# Revit family: UPA
name_source: partatom
category: Mechanical Equipment
units: mm (PartAtom-declared; Revit-internal decimal feet)

## family parameters
Always vertical = Yes
Cut with Voids When Loaded = No
OmniClass Number = 23.40.40.11.17
OmniClass Title = Refrigerated Cases
Part Type = Normal
Room Calculation Point = No
Round Connector Dimension = Use Radius
Shared = No
Work Plane-Based = Yes

## types (1)
- UPA-8'
    10" Shelf = Yes
    8" Shelf = Yes
    ANTI CON AMPS = 0 A
    BOTTOM ELECTRICAL = Yes
    BOTTOM REFRIGERATION PIPING = Yes
    CENTER LINE = 48"
    Certifications = NSF 7, UL471, CSA
    DATE = 05/11/2017
    DEFROST AMPS = 0 A
    DESIGNERS NAME = SHIDDRAMESH
    DISCHARGE AIR TEMP = 0 °F
    DISCHARGE AIR VELOCITY = -(FPM)
    DRAIN HEATERS AMPS = 0 A
    DRAIN LINE CONNECTION = SANITARY CONNECTION
    DRAIN LINE DIAMETER = 2"
    DRAIN PIPE TYPE = PVC
    DRAIN PIPING = Yes
    DRIP PAN PLUMB TYPE = HARD
    Default Elevation = 48"
    Defrost Num Day = 0
    Defrost Termination = - °F
    Defrost Type = TIMED-OFF DEFROST
    Description = Mobile Single-Deck Self-Contained Merchandiser
    Door = Door 8' : OGM-8'
    END PANEL = <By Category>
    EQUIPMENT DESCRIPTION = Mobile Single-Deck Self-Contained Merchandiser
    EQUIPMENT MARK = UPA
    Ends = Yes
    Evap Temp = 0
    GLASS = Glass
    HIGH EFFICIENCY FANS AMPS = 0 A
    Height = 49 1/4"
    Item Description = Mobile Single-Deck Self-Contained Merchandiser
    LEFT END = Yes
    LF STD END = Yes
    LIGHT AMPS = 0 A
    LIQUID LINE CONNECTION = LIQUID LINE CONNECTION
    LIQUID LINE DIAMETER = 0"
    LIQUID LINE RADIUS = 0"
    LOAD 1 CLASSIFICATION = Lighting
    LOAD 1 DESCRIPTION = LIGHTS - STANDARD POWER (SHELF or CORNICE)
    LOAD 1 PLUG TYPE = HARDWIRED
    LOAD 1 POLES = 1
    LOAD 1 VOLTAGE = 120 V
    LOAD 1 WATTAGE = 0 W
    LOAD 2 CLASSIFICATION = Motor
    LOAD 2 DESCRIPTION = HIGH EFFICIENCY FANS CONNECTION
    LOAD 2 PLUG TYPE = HARDWIRED
    LOAD 2 POLES = 1
    LOAD 2 VOLTAGE = 120 V
    LOAD 2 WATTAGE = 0 W
    LOAD 3 CLASSIFICATION = Power
    LOAD 3 DESCRIPTION = ANTI-SWEAT CONNECTION
    LOAD 3 PLUG TYPE = HARDWIRED
    LOAD 3 POLES = 1
    LOAD 3 VOLTAGE = 120 V
    LOAD 3 WATTAGE = 0 W
    LOAD 4 DESCRIPTION = DEFROST HEATER CONNECTION
    LOAD 4 PLUG TYPE = HARDWIRED
    LOAD 4 POLES = 1
    LOAD 4 VOLTAGE = 208 V
    LOAD 4 WATTAGE = 0 W
    LOAD 5 DESCRIPTION = DRAIN HEATER CONNECTION
    LOAD 5 PLUG TYPE = HARDWIRED
    LOAD 5 POLES = 1
    LOAD 5 VOLTAGE = 120 V
    LOAD 5 WATTAGE = 0 W
    Legend Number = UPA
    Length = 96"
    Load Mbh = 0
    Manufacturer = HILL PHOENIX
    Model = UPA
    Number of Doors = 2
    Number of Shelf = 3
    PAINTED METAL UPPER SHELF = PAINTED SHELVES
    POWER FACTOR = 0
    PRESSURE REGULATOR = 0.00 psi
    REAR REFRIGERATION PIPING = Yes
    REFRIGERATION PIPING = COPPER PIPE
    RT STD END = Yes
    Refgn = 8 5/8"
    Refrig Charge Lbs = -
    SANITARY PIPE SIZE = 1"
    STAINLESS STEEL = GALVANIZED STEEL
    SUCTION LINE CONNECTION = SUCTION LINE CONNECTION
    SUCTION LINE DIAMETER = 1"
    SUCTION LINE RADIUS = 0"
    Shelf distance = 48"
    TOP ELECTRICAL = Yes
    TOP REFRIGERATION PIPING = Yes
    URL = http://www.hillphoenix.com
    Width = 43 1/8"

## geometry (parser evidence)
native form markers: Blend x13, Sweep x6
no freeform markers — native parametric forms only
